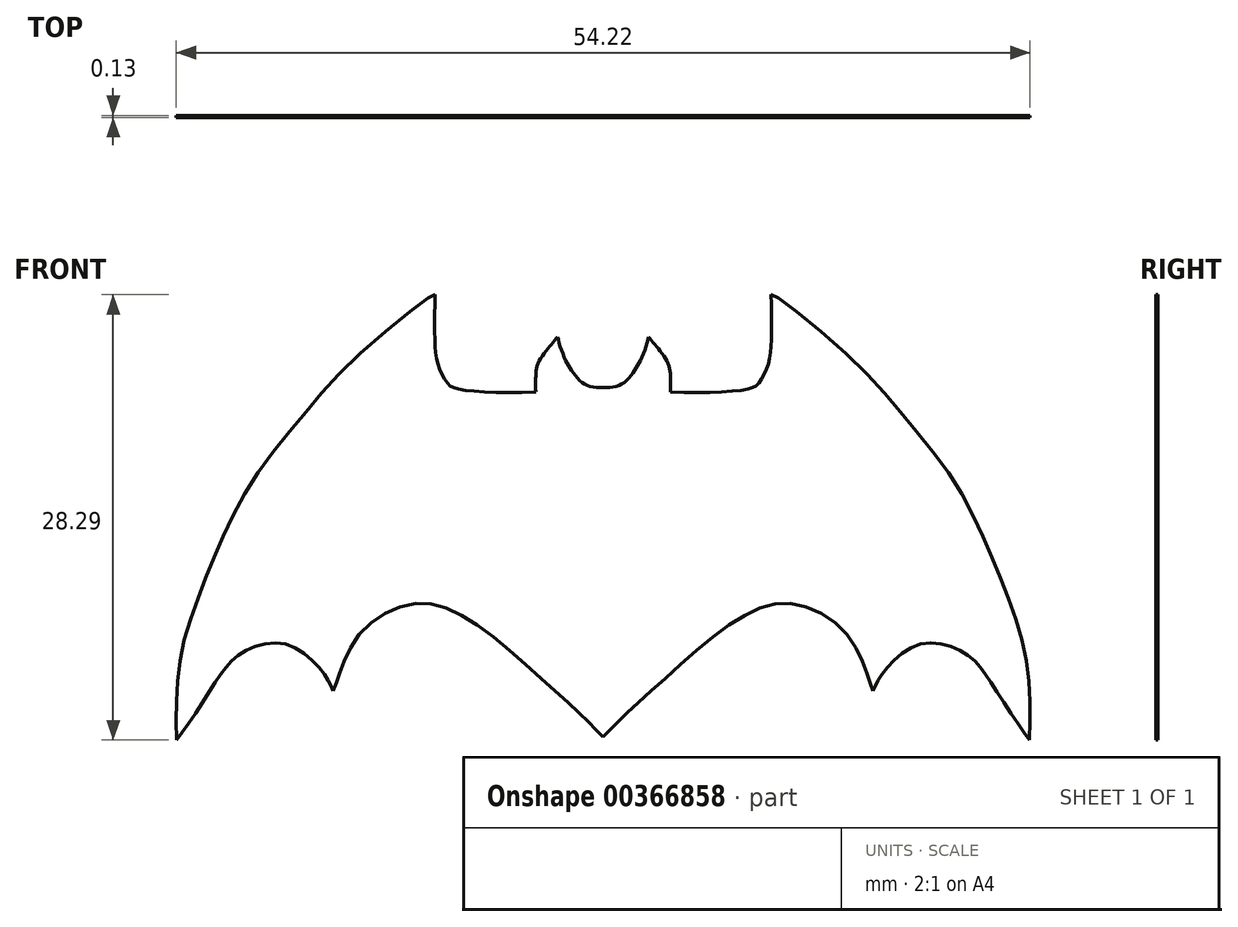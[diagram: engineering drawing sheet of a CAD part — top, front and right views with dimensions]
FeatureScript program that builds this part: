
annotation { "Feature Type Name" : "Feature", "Feature Type Description" : "" }
export const myFeature = defineFeature(function(context is Context, id is Id, definition is map)
    precondition{}
    {
        {
            var Q0;
            Q0=qCreatedBy(makeId("Front.planeOp"),FACE);
            cPlane(context, id + "F0", {"entities" : qUnion([Q0]), "cplaneType" : CPlaneType.OFFSET, "offset" : (76 / 2) * mm, "width" : 150 * mm, "height" : 150 * mm});
        }
        {
            var Q0;
            Q0=qCreatedBy(id+"F0.planeOp",FACE);
            var sketch = newSketch(context, id + "F1", { "sketchPlane" : qUnion([Q0])});
            skFitSpline(sketch, "E0", {"points": [v(-27.35, 63.02) * mm, v(-27.35, 65.86) * mm, v(-26.95, 69) * mm, v(-25.85, 72.39) * mm, v(-24.44, 75.85) * mm, v(-22.4, 79.7) * mm, v(-19.32, 83.64) * mm, v(-15.78, 87.5) * mm, v(-11.22, 91.19) * mm, v(-10.94, 91.31) * mm], "startDerivative": vector(-0.59, 28.06) * mm, "endDerivative": vector(6.03, 1.46) * mm});
            skFitSpline(sketch, "E1", {"points": [v(-10.94, 91.31) * mm, v(-10.94, 88.14) * mm, v(-10.68, 86.7) * mm, v(-10.13, 85.68) * mm, v(-9.52, 85.32) * mm, v(-4.54, 85.12) * mm], "startDerivative": vector(-0.29, -15.07) * mm, "endDerivative": vector(20.05, 0.52) * mm});
            skFitSpline(sketch, "E2", {"points": [v(-4.54, 85.12) * mm, v(-4.54, 86.1) * mm, v(-4.39, 86.94) * mm, v(-3.7, 87.96) * mm, v(-3.14, 88.63) * mm], "startDerivative": vector(-0.16, 3.64) * mm, "endDerivative": vector(2.26, 2.66) * mm});
            skFitSpline(sketch, "E3", {"points": [v(-3.14, 88.63) * mm, v(-2.7, 87.27) * mm, v(-2.18, 86.38) * mm, v(-1.38, 85.59) * mm, v(-0.26, 85.4) * mm], "startDerivative": vector(0.56, -3.93) * mm, "endDerivative": vector(4.97, -0.04) * mm});
            skFitSpline(sketch, "E4", {"points": [v(-27.35, 63.02) * mm, v(-25, 66.5) * mm, v(-23.38, 68.43) * mm, v(-20.45, 69.12) * mm, v(-18.01, 67.25) * mm, v(-17.4, 66.12) * mm], "startDerivative": vector(7.28, 9.02) * mm, "endDerivative": vector(3.2, -8.06) * mm});
            skFitSpline(sketch, "E5", {"points": [v(-17.4, 66.12) * mm, v(-16.98, 67.32) * mm, v(-15.5, 70) * mm, v(-12.2, 71.68) * mm, v(-8.83, 70.7) * mm, v(-4.24, 66.98) * mm, v(-1.4, 64.37) * mm, v(-0.26, 63.22) * mm], "startDerivative": vector(5.33, 12.94) * mm, "endDerivative": vector(9.7, -10.54) * mm});
            skLineSegment(sketch, "E6", {"start": v(-0.26, 61.07) * mm, "end": v(-0.26, 91.07) * mm, "construction": true});
            skFitSpline(sketch, "E7.MirrorCS", {"points": [v(2.62, 88.63) * mm, v(2.18, 87.27) * mm, v(1.66, 86.38) * mm, v(0.86, 85.59) * mm, v(-0.26, 85.4) * mm], "startDerivative": vector(-0.56, -3.93) * mm, "endDerivative": vector(-4.97, -0.04) * mm});
            skFitSpline(sketch, "E8.MirrorCS", {"points": [v(4.02, 85.12) * mm, v(4.02, 86.1) * mm, v(3.87, 86.94) * mm, v(3.18, 87.96) * mm, v(2.62, 88.63) * mm], "startDerivative": vector(0.16, 3.64) * mm, "endDerivative": vector(-2.26, 2.66) * mm});
            skFitSpline(sketch, "E9.MirrorCS", {"points": [v(10.42, 91.31) * mm, v(10.42, 88.14) * mm, v(10.17, 86.7) * mm, v(9.6, 85.68) * mm, v(9, 85.32) * mm, v(4.02, 85.12) * mm], "startDerivative": vector(0.29, -15.07) * mm, "endDerivative": vector(-20.05, 0.52) * mm});
            skFitSpline(sketch, "E10.MirrorCS", {"points": [v(26.83, 63.02) * mm, v(26.83, 65.86) * mm, v(26.43, 69) * mm, v(25.33, 72.39) * mm, v(23.92, 75.85) * mm, v(21.87, 79.7) * mm, v(18.8, 83.64) * mm, v(15.26, 87.5) * mm, v(10.7, 91.19) * mm, v(10.42, 91.31) * mm], "startDerivative": vector(0.59, 28.06) * mm, "endDerivative": vector(-6.03, 1.46) * mm});
            skFitSpline(sketch, "E11.MirrorCS", {"points": [v(26.83, 63.02) * mm, v(24.49, 66.5) * mm, v(22.86, 68.43) * mm, v(19.93, 69.12) * mm, v(17.5, 67.25) * mm, v(16.88, 66.12) * mm], "startDerivative": vector(-7.28, 9.02) * mm, "endDerivative": vector(-3.2, -8.06) * mm});
            skFitSpline(sketch, "E12.MirrorCS", {"points": [v(16.88, 66.12) * mm, v(16.46, 67.32) * mm, v(14.99, 70) * mm, v(11.68, 71.68) * mm, v(8.31, 70.7) * mm, v(3.72, 66.98) * mm, v(0.88, 64.37) * mm, v(-0.26, 63.22) * mm], "startDerivative": vector(-5.33, 12.94) * mm, "endDerivative": vector(-9.7, -10.54) * mm});
            skLineSegment(sketch, "E13", {"start": v(15.49, 77.98) * mm, "end": v(-18.86, 77.98) * mm, "construction": true});
            skSolve(sketch);
        }
        {
            var Q0;
            Q0 = qSketchRegion(id + "F1", true);
            extrude(context, id + "F2", {"entities" : qUnion([Q0]), "depth" : .125 * mm});
        }
    });
